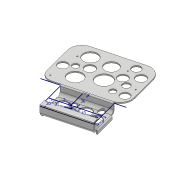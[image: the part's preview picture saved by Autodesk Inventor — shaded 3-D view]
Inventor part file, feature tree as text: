
AUTODESK INVENTOR PART (.ipt)
format: ipt  version: 2018 (Build 220112000, 112)  size: 377,344 bytes
history: native  units: mm
features: extrude x9, sketch x7, fillet x5, direct_edit x1, move_body x1
ambient origin geometry x8: Origin, YZ Plane, XZ Plane, XY Plane, X Axis, Y Axis, Z Axis, Center Point
bodies: Solid1 (feature_tree)
feature tree (23):
  sketch  "Sketch1"  dims[d1=39.5mm d2=68.0mm]
  extrude  "Extrusion1"  Depth=68.0mm
  extrude  "Extrusion2"  Depth=51.0mm
  sketch  "Sketch2"  dims[d3=98.5mm d4=51.0mm]
  extrude  "Extrusion3"  Depth=40.5mm
  extrude  "Extrusion4"  Depth=119.0mm
  extrude  "Extrusion5"  Depth=85.0mm
  extrude  "Extrusion6"  Depth=2.0mm
  fillet  "Fillet1"  Radius=2.0mm
  fillet  "Fillet2"  Radius=2.0mm
  extrude  "Extrusion7"  Depth=2.0mm TaperAngle=0.0deg
  fillet  "Fillet3"  Radius=2.0mm
  sketch  "Sketch6"  dims[d11=119.0mm d12=2.0mm d13=2.0mm d14=2.0mm]
  extrude  "Extrusion8"  Depth=2.0mm
  extrude  "Extrusion9"  Depth=2.0mm
  fillet  "Fillet4"  Radius=31.0mm
  fillet  "Fillet5"  Radius=43.0mm
  direct_edit  "Direct Edit1"
  sketch  "Sketch3"  dims[d5=107.0mm d6=40.5mm]
  sketch  "Sketch4"  dims[d7=87.5mm d8=119.0mm]
  sketch  "Sketch5"  dims[d9=30.5mm d10=85.0mm]
  sketch  "Sketch7"  dims[d15=2.0mm d16=2.0mm d17=0.0mm d18=2.0mm d19=0.0mm d20=30.0mm d21=2.0mm d22=31.0mm d23=43.0mm d24=20.0mm d25=20.0mm d26=20.0mm d27=2.0mm d28=0.0mm d29=0.0mm d30=20.0mm d31=0.0mm d32=10.0mm d33=2.0mm d34=8.0mm d35=18.0mm d36=46.0mm d37=20.0mm d38=0.0mm d39=20.0mm d40=0.0mm d41=20.0mm d42=15.0mm d43=20.0mm d44=0.0mm d45=5.0mm d46=6.0mm d47=35.0mm d48=6.0mm d49=35.0mm d50=2.0mm d51=0.0mm d52=2.0mm d53=0.0mm d54=2.0mm d55=2.0mm d56=0.0mm d57=0.0mm d58=-5.0mm]
  move_body  "Move1"
